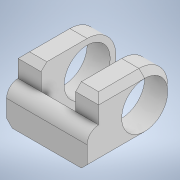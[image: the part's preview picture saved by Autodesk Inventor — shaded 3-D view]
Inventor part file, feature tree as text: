
AUTODESK INVENTOR PART (.ipt)
format: ipt  version: 2021 (Build 250183000, 183)  size: 156,160 bytes
history: native  units: mm
features: extrude x3, sketch x3, fillet x2, chamfer x1
ambient origin geometry x8: Origin, YZ Plane, XZ Plane, XY Plane, X Axis, Y Axis, Z Axis, Center Point
bodies: Solid1 (feature_tree)
feature tree (9):
  extrude  "Extrusion1"  Depth=20.0mm
  extrude  "Extrusion2"  Depth=20.0mm
  fillet  "Fillet1"  Radius=10.0mm
  fillet  "Fillet2"  Radius=50.0mm
  chamfer  "Chamfer1"  Distance=10.0mm
  extrude  "Extrusion3"  Depth=20.0mm TaperAngle=0.0deg
  sketch  "Sketch1"  dims[d0=70.0mm d1=20.0mm]
  sketch  "Sketch2"  dims[d2=30.0mm d3=20.0mm d4=10.0mm d5=50.0mm d6=0.0mm]
  sketch  "Sketch4"  dims[d7=70.0mm d8=10.0mm d9=20.0mm d10=0.0mm d11=10.0mm d13=25.0mm d14=5.0mm d15=2.0mm d16=45.0deg d17=40.0mm d18=0.0mm d19=0.0mm d20=65.0mm]
